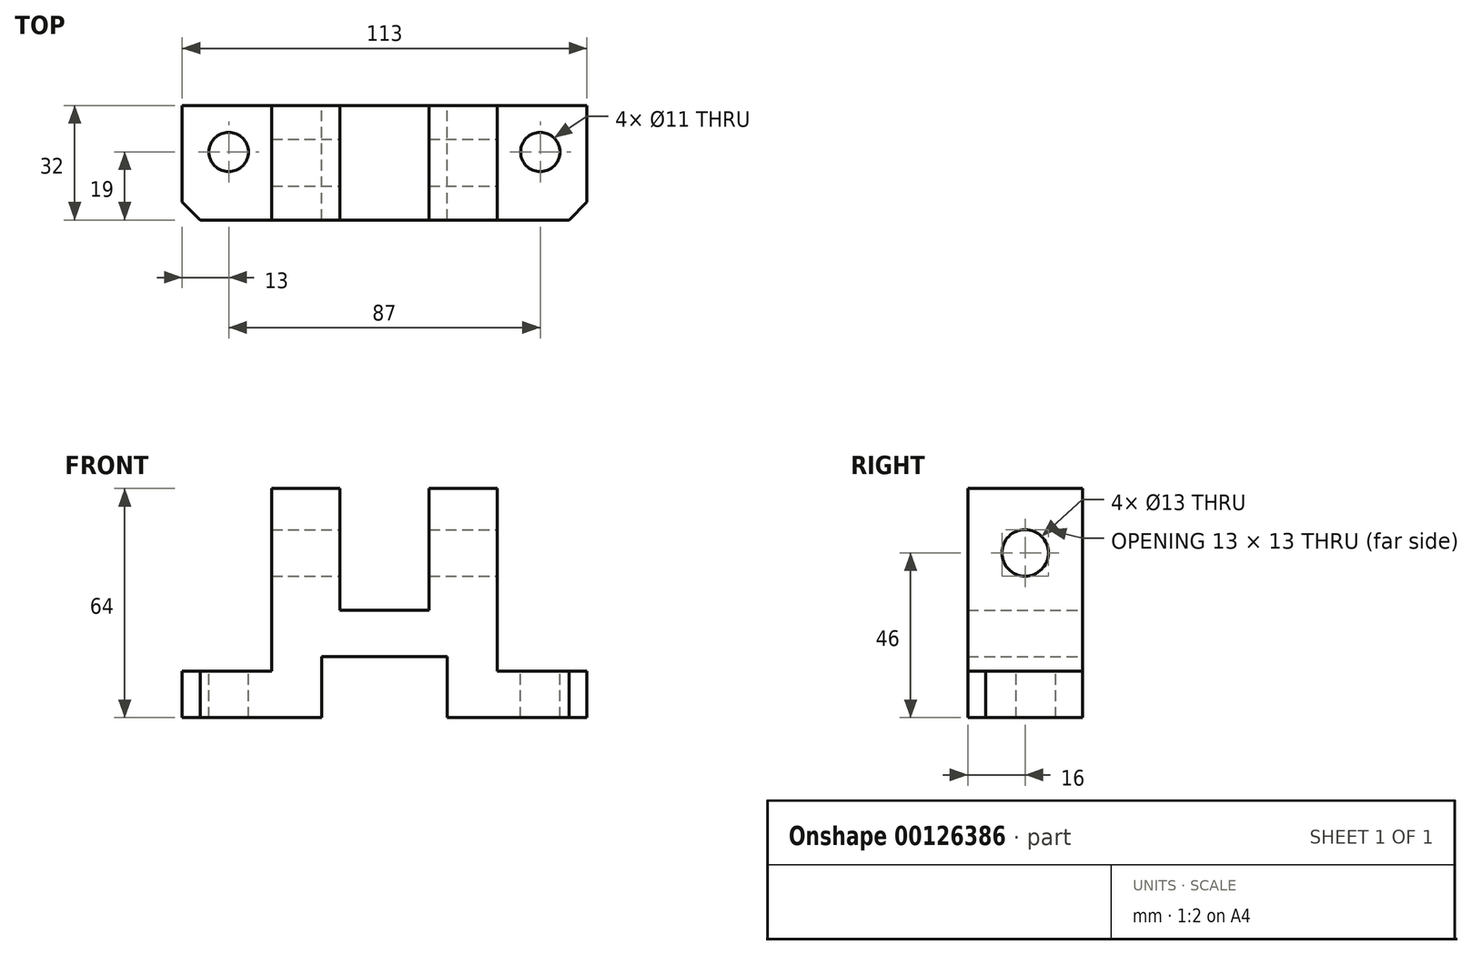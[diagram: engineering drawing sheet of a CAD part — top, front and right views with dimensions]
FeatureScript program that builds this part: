
annotation { "Feature Type Name" : "Feature", "Feature Type Description" : "" }
export const myFeature = defineFeature(function(context is Context, id is Id, definition is map)
    precondition{}
    {
        {
            var Q0;
            Q0=qCreatedBy(makeId("Front.planeOp"),FACE);
            var sketch = newSketch(context, id + "F0", { "sketchPlane" : qUnion([Q0])});
            skLineSegment(sketch, "E0", {"start": v(0, 0) * mm, "end": v(39, 0) * mm});
            skLineSegment(sketch, "E1", {"start": v(39, 0) * mm, "end": v(39, 17) * mm});
            skLineSegment(sketch, "E2", {"start": v(39, 17) * mm, "end": v(74, 17) * mm});
            skLineSegment(sketch, "E3", {"start": v(74, 17) * mm, "end": v(74, 0) * mm});
            skLineSegment(sketch, "E4", {"start": v(74, 0) * mm, "end": v(113, 0) * mm});
            skLineSegment(sketch, "E5", {"start": v(113, 0) * mm, "end": v(113, 13) * mm});
            skLineSegment(sketch, "E6", {"start": v(113, 13) * mm, "end": v(88, 13) * mm});
            skLineSegment(sketch, "E7", {"start": v(88, 13) * mm, "end": v(88, 64) * mm});
            skLineSegment(sketch, "E8", {"start": v(88, 64) * mm, "end": v(69, 64) * mm});
            skLineSegment(sketch, "E9", {"start": v(69, 64) * mm, "end": v(69, 30) * mm});
            skLineSegment(sketch, "E10", {"start": v(69, 30) * mm, "end": v(44, 30) * mm});
            skLineSegment(sketch, "E11", {"start": v(44, 30) * mm, "end": v(44, 64) * mm});
            skLineSegment(sketch, "E12", {"start": v(44, 64) * mm, "end": v(25, 64) * mm});
            skLineSegment(sketch, "E13", {"start": v(25, 64) * mm, "end": v(25, 13) * mm});
            skLineSegment(sketch, "E14", {"start": v(25, 13) * mm, "end": v(0, 13) * mm});
            skLineSegment(sketch, "E15", {"start": v(0, 13) * mm, "end": v(0, 0) * mm});
            skSolve(sketch);
        }
        {
            var Q0;
            Q0 = qSketchRegion(id + "F0", true);
            extrude(context, id + "F1", {"entities" : qUnion([Q0]), "depth" : 32 * mm});
        }
        {
            var Q0;
            Q0=makeQuery(id+"F1.opExtrude","CAP_EDGE",EDGE,{"disambiguationData":[OSD([sQuery(id+"F0.wireOp",EDGE,"E5")])],"isStart":false});
            chamfer(context, id + "F2", {"entities" : qUnion([Q0]), "width" : 5 * mm, "tangentPropagation" : true});
        }
        {
            var Q0;
            Q0=makeQuery(id+"F1.opExtrude","CAP_EDGE",EDGE,{"disambiguationData":[OSD([sQuery(id+"F0.wireOp",EDGE,"E15")])],"isStart":false});
            chamfer(context, id + "F3", {"entities" : qUnion([Q0]), "width" : 5 * mm, "tangentPropagation" : true});
        }
        {
            var Q0;
            Q0=makeQuery(id+"F1.opExtrude","SWEPT_FACE",FACE,{"disambiguationData":[OSD([sQuery(id+"F0.wireOp",EDGE,"E7")])]});
            var sketch = newSketch(context, id + "F4", { "sketchPlane" : qUnion([Q0])});
            skCircle(sketch, "E16", {"center": v(-16, 46) * mm, "radius": 6.5 * mm});
            skSolve(sketch);
        }
        {
            var Q0;
            Q0 = qSketchRegion(id + "F4", true);
            extrude(context, id + "F5", {"entities" : qUnion([Q0]), "operationType" : NewBodyOperationType.REMOVE, "endBound" : BoundingType.THROUGH_ALL, "oppositeDirection" : true, "depth" : 25 * mm});
        }
        {
            var Q0;
            Q0=makeQuery(id+"F1.opExtrude","SWEPT_FACE",FACE,{"disambiguationData":[OSD([sQuery(id+"F0.wireOp",EDGE,"E14")])]});
            var sketch = newSketch(context, id + "F6", { "sketchPlane" : qUnion([Q0])});
            skCircle(sketch, "E17", {"center": v(13, -13) * mm, "radius": 5.5 * mm});
            skCircle(sketch, "E18", {"center": v(100, -13) * mm, "radius": 5.5 * mm});
            skSolve(sketch);
        }
        {
            var Q0;
            Q0 = qSketchRegion(id + "F6", true);
            extrude(context, id + "F7", {"entities" : qUnion([Q0]), "operationType" : NewBodyOperationType.REMOVE, "endBound" : BoundingType.THROUGH_ALL, "oppositeDirection" : true, "depth" : 25 * mm});
        }
    });
